# Revit family: BM_GenericModel_WaterCooler
name_source: partatom
category: Generic Models
units: mm (PartAtom-declared; Revit-internal decimal feet)

## family parameters
Always vertical = Yes
Can host rebar = No
Cut with Voids When Loaded = No
Maintain Annotation Orientation = No
OmniClass Number = 23.40.40.14.24
OmniClass Title = Food Dispensing Equipment
Part Type = Normal
Room Calculation Point = No
Round Connector Dimension = Use Diameter
Shared = No
Work Plane-Based = No

## types (1)
- Water Cooler
    Default Elevation = 0 mm  [stored 0 ft]
    Description = A water dispenser, known as water cooler is a machine that cools or heats up and dispenses water with a refrigeration unit.
    Height without Bottle = 830 mm
    Model = Water Cooler
    Overall Height = 1200 mm
    Overall Length = 300 mm
    Overall Width = 280 mm  [stored 0.918635 ft]
    Type Comments = Water Cooler
    Volts = 120 V

note: [stored X ft] marks values corroborated as IEEE doubles in the binary element streams (Revit-internal decimal feet)

## geometry (parser evidence)
native form markers: Sweep x2
no freeform markers — native parametric forms only
